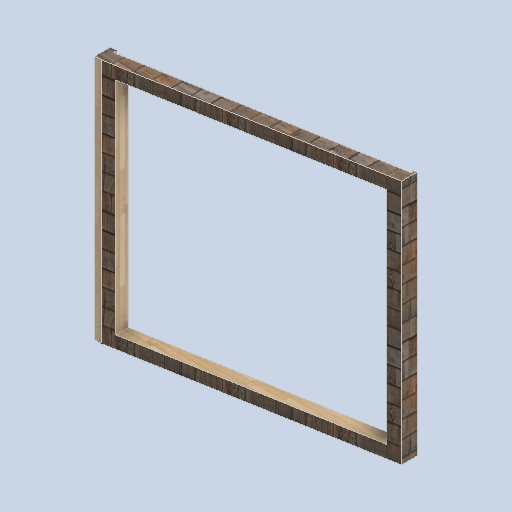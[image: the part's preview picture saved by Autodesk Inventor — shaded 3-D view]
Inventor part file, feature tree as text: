
AUTODESK INVENTOR PART (.ipt)
format: ipt  version: 2024.2 (Build 282272000, 272)  size: 199,168 bytes
history: native  units: in
note: dims shown in document units (in); Inventor stores cm internally (conversion verified against a paired STEP export)
features: plane x4, other x3, sketch x3
ambient origin geometry x8: Origin, YZ Plane, XZ Plane, XY Plane, X Axis, Y Axis, Z Axis, Center Point
bodies: Solid1 (feature_tree)
feature tree (10):
  other  "eave_frame_side__MIR.ipt"
  other  "Solid1::eave_frame_side__MIR.ipt"
  other  "TaggingFeature1"
  sketch  "Sketch1"  dims[d0=0.3937in]
  sketch  "Sketch6"
  sketch  "Sketch11"
  plane  "Work Plane1"
  plane  "Work Plane2"
  plane  "Work Plane3"
  plane  "Work Plane4"
